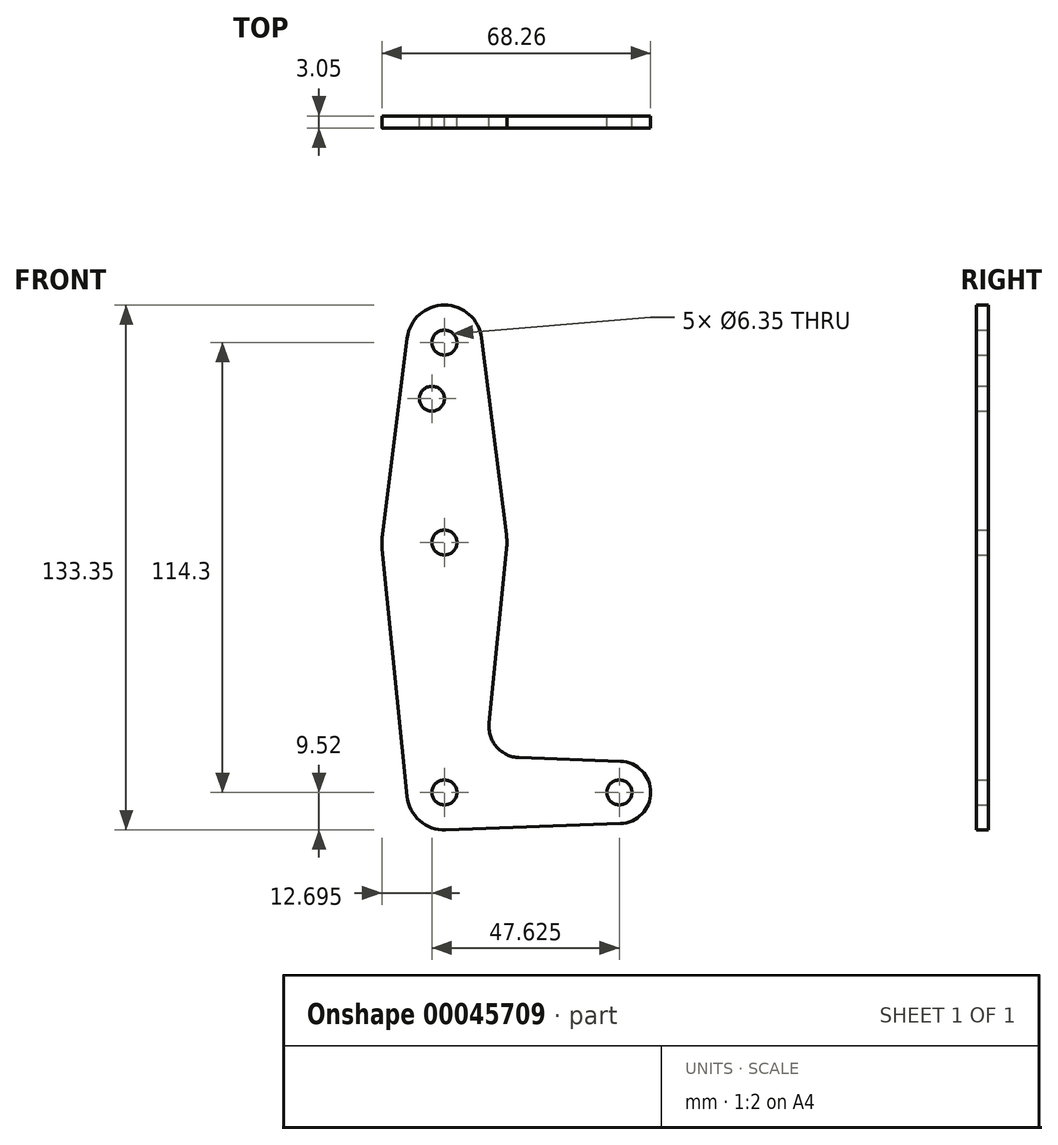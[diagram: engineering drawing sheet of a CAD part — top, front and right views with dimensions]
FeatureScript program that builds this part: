
annotation { "Feature Type Name" : "Feature", "Feature Type Description" : "" }
export const myFeature = defineFeature(function(context is Context, id is Id, definition is map)
    precondition{}
    {
        {
            var Q0;
            Q0=qCreatedBy(makeId("Front.planeOp"),FACE);
            var sketch = newSketch(context, id + "F0", { "sketchPlane" : qUnion([Q0])});
            skLineSegment(sketch, "E0", {"start": v(44.45, 0) * mm, "end": v(0, 0) * mm, "construction": true});
            skLineSegment(sketch, "E1", {"start": v(0, 0) * mm, "end": v(0, 114.3) * mm, "construction": true});
            skCircle(sketch, "E2", {"center": v(0, 0) * mm, "radius": 9.53 * mm});
            skCircle(sketch, "E3", {"center": v(44.45, 0) * mm, "radius": 7.94 * mm});
            skCircle(sketch, "E4", {"center": v(0, 63.5) * mm, "radius": 15.88 * mm});
            skCircle(sketch, "E5", {"center": v(0, 114.3) * mm, "radius": 9.53 * mm});
            skLineSegment(sketch, "E6", {"start": v(-9.45, 115.5) * mm, "end": v(-15.75, 65.48) * mm});
            skLineSegment(sketch, "E7", {"start": v(-15.8, 61.91) * mm, "end": v(-9.48, -0.95) * mm});
            skLineSegment(sketch, "E8", {"start": v(11.34, 17.6) * mm, "end": v(15.8, 61.91) * mm});
            skLineSegment(sketch, "E9", {"start": v(15.75, 65.48) * mm, "end": v(9.45, 115.5) * mm});
            skLineSegment(sketch, "E10", {"start": v(18.97, 8.85) * mm, "end": v(44.73, 7.93) * mm});
            skLineSegment(sketch, "E11", {"start": v(0.34, -9.52) * mm, "end": v(44.73, -7.93) * mm});
            skCircle(sketch, "E12", {"center": v(0, 114.3) * mm, "radius": 3.18 * mm});
            skCircle(sketch, "E13", {"center": v(-3.18, 100.03) * mm, "radius": 3.18 * mm});
            skCircle(sketch, "E14", {"center": v(0, 63.5) * mm, "radius": 3.18 * mm});
            skCircle(sketch, "E15", {"center": v(44.45, 0) * mm, "radius": 3.18 * mm});
            skCircle(sketch, "E16", {"center": v(0, 0) * mm, "radius": 3.18 * mm});
            skArc(sketch, "E17.filletArc", {"start": v(11.34, 17.6) * mm, "mid": v(13.26, 11.57) * mm, "end": v(18.97, 8.85) * mm});
            skSolve(sketch);
        }
        {
            var Q0;
            Q0 = qSketchRegion(id + "F0", true);
            extrude(context, id + "F1", {"entities" : qUnion([Q0]), "depth" : 3.05 * mm});
        }
    });
